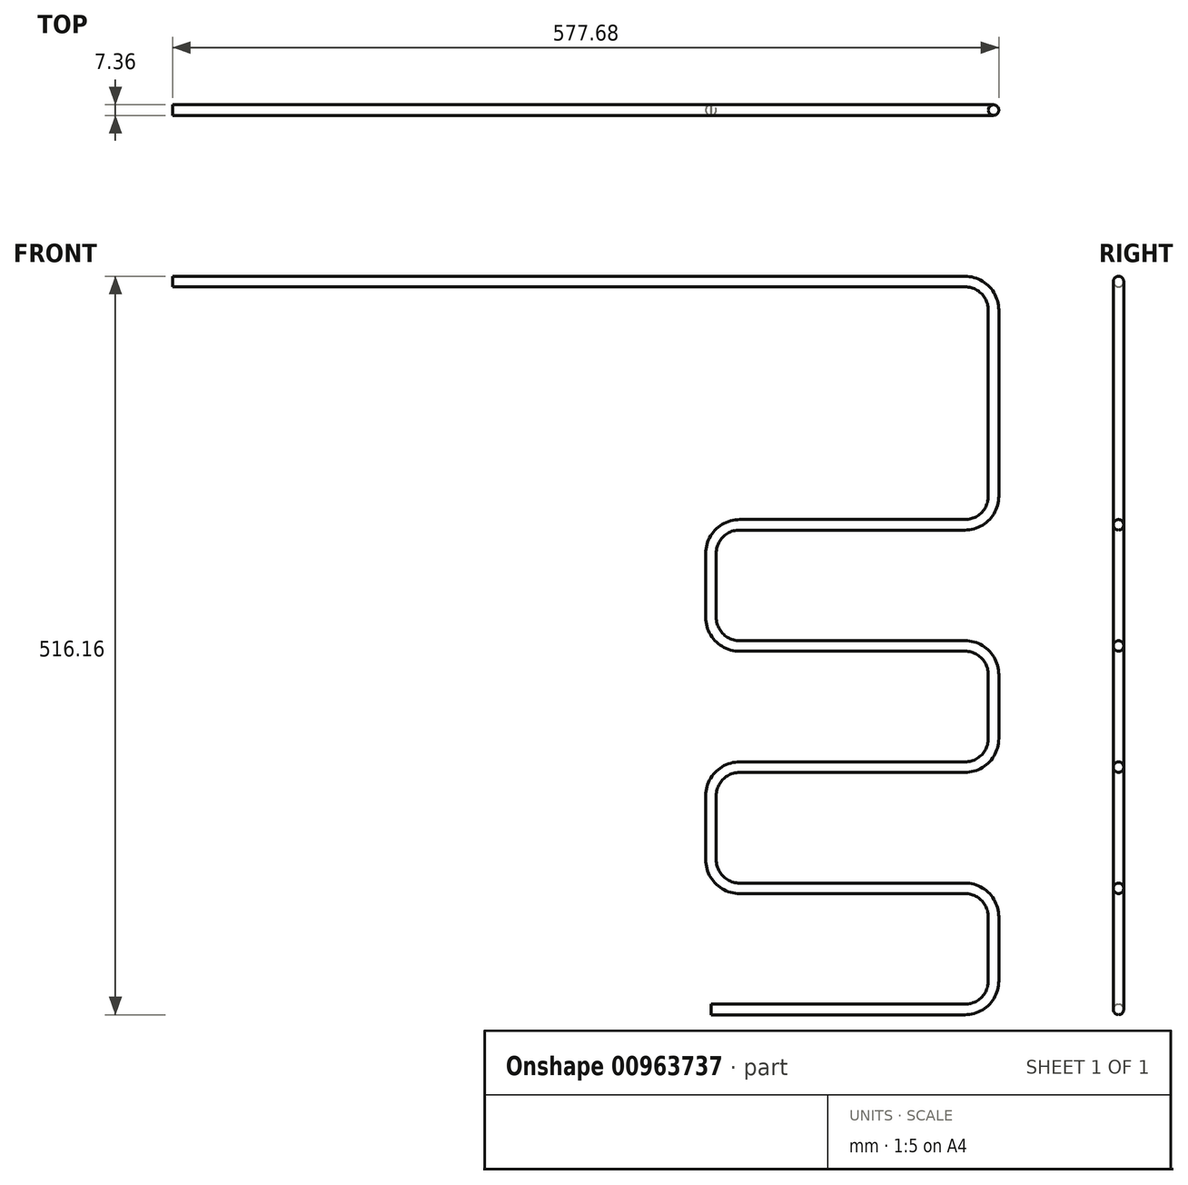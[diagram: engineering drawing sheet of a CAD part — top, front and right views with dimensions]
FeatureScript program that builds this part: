
annotation { "Feature Type Name" : "Feature", "Feature Type Description" : "" }
export const myFeature = defineFeature(function(context is Context, id is Id, definition is map)
    precondition{}
    {
        {
            var Q0;
            Q0=qCreatedBy(makeId("Front.planeOp"),FACE);
            var sketch = newSketch(context, id + "F0", { "sketchPlane" : qUnion([Q0])});
            skLineSegment(sketch, "E0", {"start": v(0, 0) * mm, "end": v(554, 0) * mm});
            skLineSegment(sketch, "E1", {"start": v(574, -20) * mm, "end": v(574, -150) * mm});
            skLineSegment(sketch, "E2", {"start": v(554, -170) * mm, "end": v(396.4, -170) * mm});
            skLineSegment(sketch, "E3", {"start": v(376.4, -190) * mm, "end": v(376.4, -234.7) * mm});
            skLineSegment(sketch, "E4", {"start": v(396.4, -254.7) * mm, "end": v(554, -254.7) * mm});
            skLineSegment(sketch, "E5", {"start": v(574, -274.7) * mm, "end": v(574, -319.4) * mm});
            skLineSegment(sketch, "E6", {"start": v(554, -339.4) * mm, "end": v(396.4, -339.4) * mm});
            skLineSegment(sketch, "E7", {"start": v(376.4, -359.4) * mm, "end": v(376.4, -404.1) * mm});
            skLineSegment(sketch, "E8", {"start": v(396.4, -424.1) * mm, "end": v(554, -424.1) * mm});
            skLineSegment(sketch, "E9", {"start": v(574, -444.1) * mm, "end": v(574, -488.8) * mm});
            skLineSegment(sketch, "E10", {"start": v(554, -508.8) * mm, "end": v(376.4, -508.8) * mm});
            skPoint(sketch, "E11.visualSharp", {"position": v(574, 0) * mm});
            skArc(sketch, "E11.filletArc", {"start": v(574, -20) * mm, "mid": v(568.14, -5.86) * mm, "end": v(554, 0) * mm});
            skPoint(sketch, "E12.visualSharp", {"position": v(574, -170) * mm});
            skArc(sketch, "E12.filletArc", {"start": v(554, -170) * mm, "mid": v(568.14, -164.14) * mm, "end": v(574, -150) * mm});
            skPoint(sketch, "E13.visualSharp", {"position": v(376.4, -170) * mm});
            skArc(sketch, "E13.filletArc", {"start": v(396.4, -170) * mm, "mid": v(382.26, -175.86) * mm, "end": v(376.4, -190) * mm});
            skPoint(sketch, "E14.visualSharp", {"position": v(574, -254.7) * mm});
            skArc(sketch, "E14.filletArc", {"start": v(574, -274.7) * mm, "mid": v(568.14, -260.56) * mm, "end": v(554, -254.7) * mm});
            skPoint(sketch, "E15.visualSharp", {"position": v(574, -339.4) * mm});
            skArc(sketch, "E15.filletArc", {"start": v(554, -339.4) * mm, "mid": v(568.14, -333.54) * mm, "end": v(574, -319.4) * mm});
            skPoint(sketch, "E16.visualSharp", {"position": v(376.4, -339.4) * mm});
            skArc(sketch, "E16.filletArc", {"start": v(396.4, -339.4) * mm, "mid": v(382.26, -345.26) * mm, "end": v(376.4, -359.4) * mm});
            skPoint(sketch, "E17.visualSharp", {"position": v(376.4, -424.1) * mm});
            skArc(sketch, "E17.filletArc", {"start": v(376.4, -404.1) * mm, "mid": v(382.26, -418.24) * mm, "end": v(396.4, -424.1) * mm});
            skPoint(sketch, "E18.visualSharp", {"position": v(574, -424.1) * mm});
            skArc(sketch, "E18.filletArc", {"start": v(574, -444.1) * mm, "mid": v(568.14, -429.96) * mm, "end": v(554, -424.1) * mm});
            skPoint(sketch, "E19.visualSharp", {"position": v(376.4, -254.7) * mm});
            skArc(sketch, "E19.filletArc", {"start": v(376.4, -234.7) * mm, "mid": v(382.26, -248.84) * mm, "end": v(396.4, -254.7) * mm});
            skPoint(sketch, "E20.visualSharp", {"position": v(574, -508.8) * mm});
            skArc(sketch, "E20.filletArc", {"start": v(554, -508.8) * mm, "mid": v(568.14, -502.94) * mm, "end": v(574, -488.8) * mm});
            skSolve(sketch);
        }
        {
            var Q0;
            Q0=qCreatedBy(makeId("Right.planeOp"),FACE);
            var sketch = newSketch(context, id + "F1", { "sketchPlane" : qUnion([Q0])});
            skCircle(sketch, "E21", {"center": v(0, 0) * mm, "radius": 3.67 * mm});
            skSolve(sketch);
        }
        {
            var Q0;
            Q0=makeQuery(id+"F1.imprint","IMPRINT",FACE,{"disambiguationData":[TD([[makeQuery(id+"F1.imprint","IMPRINT",EDGE,{"derivedFrom":sQuery(id+"F1.wireOp",EDGE,"E21")}),1.0]])]});
            var Q1;
            Q1=sQuery(id+"F0.wireOp",EDGE,"E0");
            var Q2;
            Q2=sQuery(id+"F0.wireOp",EDGE,"E11.filletArc");
            var Q3;
            Q3=sQuery(id+"F0.wireOp",EDGE,"E1");
            var Q4;
            Q4=sQuery(id+"F0.wireOp",EDGE,"E12.filletArc");
            var Q5;
            Q5=sQuery(id+"F0.wireOp",EDGE,"E2");
            var Q6;
            Q6=sQuery(id+"F0.wireOp",EDGE,"E13.filletArc");
            var Q7;
            Q7=sQuery(id+"F0.wireOp",EDGE,"E3");
            var Q8;
            Q8=sQuery(id+"F0.wireOp",EDGE,"E19.filletArc");
            var Q9;
            Q9=sQuery(id+"F0.wireOp",EDGE,"E4");
            var Q10;
            Q10=sQuery(id+"F0.wireOp",EDGE,"E14.filletArc");
            var Q11;
            Q11=sQuery(id+"F0.wireOp",EDGE,"E5");
            var Q12;
            Q12=sQuery(id+"F0.wireOp",EDGE,"E15.filletArc");
            var Q13;
            Q13=sQuery(id+"F0.wireOp",EDGE,"E6");
            var Q14;
            Q14=sQuery(id+"F0.wireOp",EDGE,"E16.filletArc");
            var Q15;
            Q15=sQuery(id+"F0.wireOp",EDGE,"E7");
            var Q16;
            Q16=sQuery(id+"F0.wireOp",EDGE,"E17.filletArc");
            var Q17;
            Q17=sQuery(id+"F0.wireOp",EDGE,"E8");
            var Q18;
            Q18=sQuery(id+"F0.wireOp",EDGE,"E18.filletArc");
            var Q19;
            Q19=sQuery(id+"F0.wireOp",EDGE,"E9");
            var Q20;
            Q20=sQuery(id+"F0.wireOp",EDGE,"E20.filletArc");
            var Q21;
            Q21=sQuery(id+"F0.wireOp",EDGE,"E10");
            sweep(context, id + "F2", {"profiles" : qUnion([Q0]), "path" : qUnion([Q1, Q2, Q3, Q4, Q5, Q6, Q7, Q8, Q9, Q10, Q11, Q12, Q13, Q14, Q15, Q16, Q17, Q18, Q19, Q20, Q21])});
        }
    });
